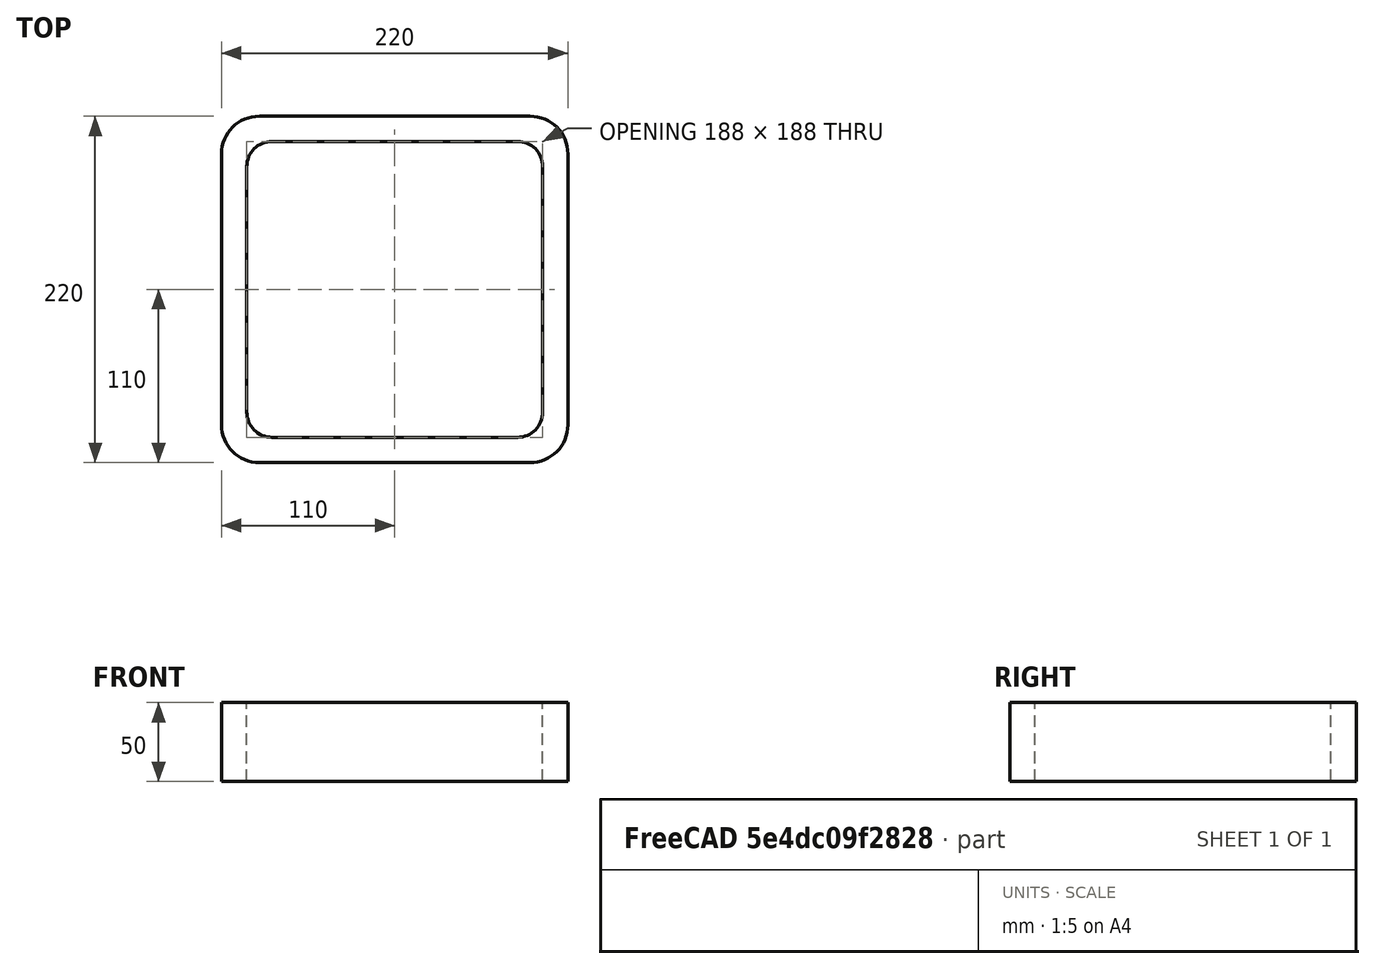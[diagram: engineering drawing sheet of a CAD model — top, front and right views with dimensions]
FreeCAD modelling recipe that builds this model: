
FCSTD DOCUMENT  (FreeCAD 0.15R4671 (Git))
Label: Square hollow section 220x220x16 EN10219 S235JRH
License: All rights reserved
LicenseURL: http://en.wikipedia.org/wiki/All_rights_reserved
objects: Sketcher::SketchObject×1, Part::Extrusion×1
note: 2 computed .brp shape members not serialized (recipe doc carries the construction recipe); baked Part::Feature solids carry a one-line shape summary decoded from their .brp

FEATURE [Sketcher::SketchObject] Sketch
  sketch-geometry (16):
    g0: LineSegment StartX=-78 StartY=94 StartZ=0 EndX=78 EndY=94 EndZ=0
    g1: LineSegment StartX=94 StartY=78 StartZ=0 EndX=94 EndY=-78 EndZ=0
    g2: LineSegment StartX=78 StartY=-94 StartZ=0 EndX=-78 EndY=-94 EndZ=0
    g3: LineSegment StartX=-94 StartY=-78 StartZ=0 EndX=-94 EndY=78 EndZ=0
    g4: LineSegment StartX=-86 StartY=110 StartZ=0 EndX=86 EndY=110 EndZ=0
    g5: LineSegment StartX=110 StartY=86 StartZ=0 EndX=110 EndY=-86 EndZ=0
    g6: LineSegment StartX=86 StartY=-110 StartZ=0 EndX=-86 EndY=-110 EndZ=0
    g7: LineSegment StartX=-110 StartY=-86 StartZ=0 EndX=-110 EndY=86 EndZ=0
    g8: ArcOfCircle CenterX=-78 CenterY=78 CenterZ=0 NormalX=0 NormalY=0 NormalZ=1 Radius=16 StartAngle=1.5708 EndAngle=3.14159
    g9: ArcOfCircle CenterX=78 CenterY=78 CenterZ=0 NormalX=0 NormalY=0 NormalZ=1 Radius=16 StartAngle=0 EndAngle=1.5708
    g10: ArcOfCircle CenterX=78 CenterY=-78 CenterZ=0 NormalX=0 NormalY=0 NormalZ=1 Radius=16 StartAngle=4.71239 EndAngle=6.28319
    g11: ArcOfCircle CenterX=-78 CenterY=-78 CenterZ=0 NormalX=0 NormalY=0 NormalZ=1 Radius=16 StartAngle=3.14159 EndAngle=4.71239
    g12: ArcOfCircle CenterX=86 CenterY=86 CenterZ=0 NormalX=0 NormalY=0 NormalZ=1 Radius=24 StartAngle=0 EndAngle=1.5708
    g13: ArcOfCircle CenterX=86 CenterY=-86 CenterZ=0 NormalX=0 NormalY=0 NormalZ=1 Radius=24 StartAngle=4.71239 EndAngle=6.28319
    g14: ArcOfCircle CenterX=-86 CenterY=-86 CenterZ=0 NormalX=0 NormalY=0 NormalZ=1 Radius=24 StartAngle=3.14159 EndAngle=4.71239
    g15: ArcOfCircle CenterX=-86 CenterY=86 CenterZ=0 NormalX=0 NormalY=0 NormalZ=1 Radius=24 StartAngle=1.5708 EndAngle=3.14159
  constraints (36):
    c: Horizontal(g2)
    c: Vertical(g3)
    c: Horizontal(g6)
    c: Vertical(g7)
    c: Tangent(g3,g8) = 1.5708
    c: Tangent(g0,g8) = 1.5708
    c: Tangent(g0,g9) = 1.5708
    c: Tangent(g1,g9) = 1.5708
    c: Tangent(g1,g10) = 1.5708
    c: Tangent(g2,g10) = 1.5708
    c: Tangent(g2,g11) = 1.5708
    c: Tangent(g3,g11) = 1.5708
    c: Tangent(g4,g12) = 1.5708
    c: Tangent(g5,g12) = 1.5708
    c: Tangent(g5,g13) = 1.5708
    c: Tangent(g6,g13) = 1.5708
    c: Tangent(g6,g14) = 1.5708
    c: Tangent(g7,g14) = 1.5708
    c: Tangent(g7,g15) = 1.5708
    c: Tangent(g4,g15) = 1.5708
    c: Equal(g9,g8)
    c: Equal(g9,g11)
    c: Equal(g9,g10)
    c: Equal(g12,g15)
    c: Equal(g12,g14)
    c: Equal(g12,g13)
    c: Symmetric(g4,g6,g-1)
    c: Symmetric(g7,g5,g-2)
    c: DistanceY(g4,g6) = -220
    c: DistanceX(g7,g5) = 220
    c: Symmetric(g3,g1,g-2)
    c: Symmetric(g0,g2,g-1)
    c: DistanceY(g0,g4) = 16
    c: DistanceX(g5,g1) = -16
    c: Radius(g9) = 16
    c: Radius(g12) = 24
FEATURE [Part::Extrusion] Extrude  label="Square hollow section 220x220x16 EN10219 S235JRH"
  Base = -> Sketch
  Dir = (0,0,50)
  Solid = true
